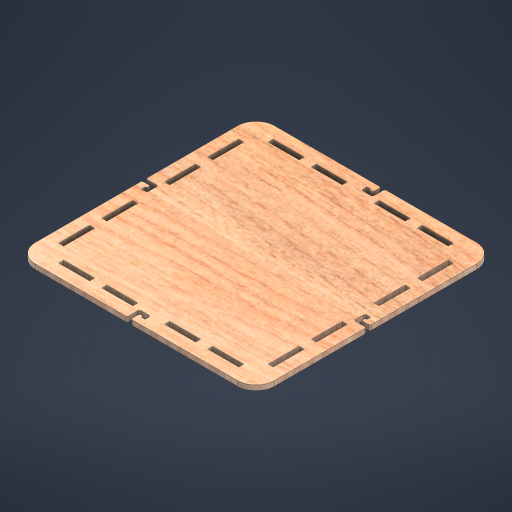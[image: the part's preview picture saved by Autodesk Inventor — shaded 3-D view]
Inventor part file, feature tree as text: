
AUTODESK INVENTOR PART (.ipt)
format: ipt  version: 2024.1 (Build 281209000, 209)  size: 551,424 bytes
history: native  units: mm
features: extrude x1, fillet x1, sketch x1
ambient origin geometry x8: Origin, YZ Plane, XZ Plane, XY Plane, X Axis, Y Axis, Z Axis, Center Point
bodies: Solid1 (feature_tree)
feature tree (3):
  extrude  "Extrusion1"  Depth=4.0mm
  fillet  "Fillet1"  Radius=10.0mm
  sketch  "Sketch1"  dims[d0=25.0mm d1=4.0mm d4=10.0mm d5=13.0mm d6=10.0mm d7=10.0mm d8=10.0mm d9=13.0mm d10=40.0mm d12=360.0deg d14=10.0mm d15=10.0mm d16=15.0mm d17=7.0mm d18=3.0mm d19=6.0mm d20=3.0mm d21=1.5mm d22=40.0mm d24=360.0deg d26=4.0mm d27=0.0mm d28=1.5mm]
